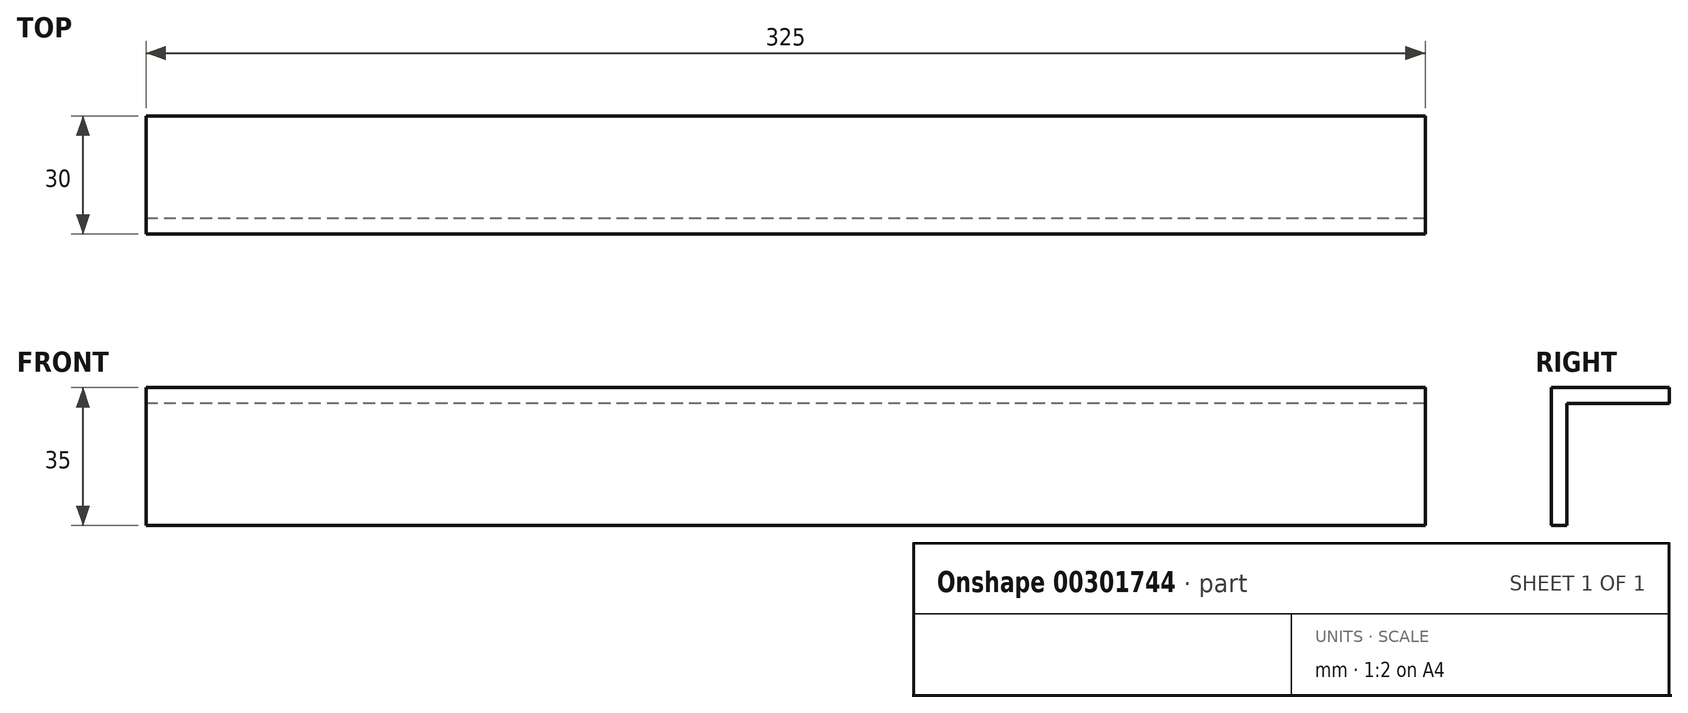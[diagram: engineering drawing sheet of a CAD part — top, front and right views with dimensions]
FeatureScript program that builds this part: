
annotation { "Feature Type Name" : "Feature", "Feature Type Description" : "" }
export const myFeature = defineFeature(function(context is Context, id is Id, definition is map)
    precondition{}
    {
        {
            var Q0;
            Q0=qCreatedBy(makeId("Right.planeOp"),FACE);
            var sketch = newSketch(context, id + "F0", { "sketchPlane" : qUnion([Q0])});
            skLineSegment(sketch, "E0", {"start": v(0, 0) * mm, "end": v(0, -35) * mm});
            skLineSegment(sketch, "E1", {"start": v(0, -35) * mm, "end": v(4, -35) * mm});
            skLineSegment(sketch, "E2", {"start": v(4, -35) * mm, "end": v(4, -4) * mm});
            skLineSegment(sketch, "E3", {"start": v(4, -4) * mm, "end": v(30, -4) * mm});
            skLineSegment(sketch, "E4", {"start": v(30, -4) * mm, "end": v(30, 0) * mm});
            skLineSegment(sketch, "E5", {"start": v(30, 0) * mm, "end": v(0, 0) * mm});
            skSolve(sketch);
        }
        {
            var Q0;
            Q0=makeQuery(id+"F0.imprint","IMPRINT",FACE,{"disambiguationData":[TD([[makeQuery(id+"F0.imprint","IMPRINT",EDGE,{"derivedFrom":sQuery(id+"F0.wireOp",EDGE,"E0")}),1.0]])]});
            extrude(context, id + "F1", {"entities" : qUnion([Q0]), "depth" : 325 * mm});
        }
    });
